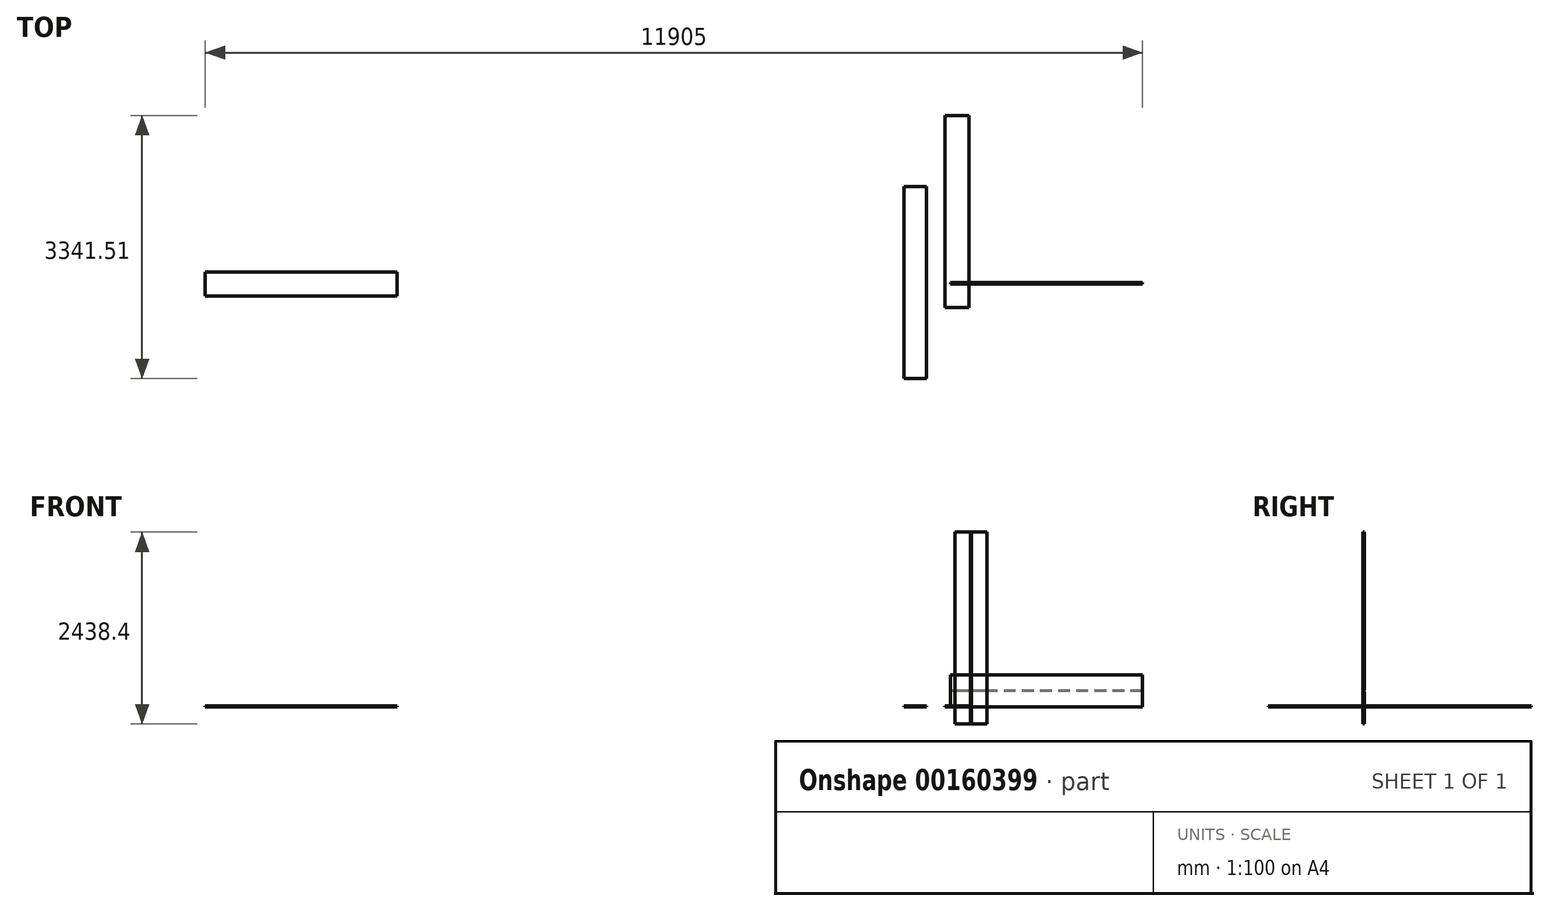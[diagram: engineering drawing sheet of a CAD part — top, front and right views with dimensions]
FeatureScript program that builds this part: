
annotation { "Feature Type Name" : "Feature", "Feature Type Description" : "" }
export const myFeature = defineFeature(function(context is Context, id is Id, definition is map)
    precondition{}
    {
        {
            var Q0;
            Q0=qCreatedBy(makeId("Top.planeOp"),FACE);
            var sketch = newSketch(context, id + "F0", { "sketchPlane" : qUnion([Q0])});
            skLineSegment(sketch, "E0.bottom", {"start": v(-311.98, 2122.24) * mm, "end": v(-7.18, 2122.24) * mm});
            skLineSegment(sketch, "E0.top", {"start": v(-311.98, -316.16) * mm, "end": v(-7.18, -316.16) * mm});
            skLineSegment(sketch, "E0.left", {"start": v(-311.98, 2122.24) * mm, "end": v(-311.98, -316.16) * mm});
            skLineSegment(sketch, "E0.right", {"start": v(-7.18, 2122.24) * mm, "end": v(-7.18, -316.16) * mm});
            skSolve(sketch);
        }
        {
            var Q0;
            Q0=makeQuery(id+"F0.imprint","IMPRINT",FACE,{"disambiguationData":[TD([[makeQuery(id+"F0.imprint","IMPRINT",EDGE,{"derivedFrom":sQuery(id+"F0.wireOp",EDGE,"E0.bottom")}),-1.0]])]});
            extrude(context, id + "F1", {"entities" : qUnion([Q0]), "depth" : 12.7 * mm});
        }
        {
            var Q0;
            Q0=qCreatedBy(makeId("Top.planeOp"),FACE);
            var sketch = newSketch(context, id + "F2", { "sketchPlane" : qUnion([Q0])});
            skLineSegment(sketch, "E1.bottom", {"start": v(-9710.38, -172.02) * mm, "end": v(-7271.98, -172.02) * mm});
            skLineSegment(sketch, "E1.top", {"start": v(-9710.38, 132.78) * mm, "end": v(-7271.98, 132.78) * mm});
            skLineSegment(sketch, "E1.left", {"start": v(-9710.38, -172.02) * mm, "end": v(-9710.38, 132.78) * mm});
            skLineSegment(sketch, "E1.right", {"start": v(-7271.98, -172.02) * mm, "end": v(-7271.98, 132.78) * mm});
            skSolve(sketch);
        }
        {
            var Q0;
            Q0 = qSketchRegion(id + "F2", true);
            extrude(context, id + "F3", {"entities" : qUnion([Q0]), "depth" : 12.7 * mm});
        }
        {
            var Q0;
            Q0=qCreatedBy(makeId("Front.planeOp"),FACE);
            var sketch = newSketch(context, id + "F4", { "sketchPlane" : qUnion([Q0])});
            skLineSegment(sketch, "E2.bottom", {"start": v(221, 2220.65) * mm, "end": v(-185.4, 2220.65) * mm});
            skLineSegment(sketch, "E2.top", {"start": v(221, -217.75) * mm, "end": v(-185.4, -217.75) * mm});
            skLineSegment(sketch, "E2.left", {"start": v(221, 2220.65) * mm, "end": v(221, -217.75) * mm});
            skLineSegment(sketch, "E2.right", {"start": v(-185.4, 2220.65) * mm, "end": v(-185.4, -217.75) * mm});
            skSolve(sketch);
        }
        {
            var Q0;
            Q0 = qSketchRegion(id + "F4", true);
            extrude(context, id + "F5", {"entities" : qUnion([Q0]), "depth" : 19.05 * mm});
        }
        {
            var Q0;
            Q0=makeQuery(id+"F5.opExtrude","CAP_FACE",FACE,{"disambiguationData":[OSD([sQuery(id+"F4.wireOp",EDGE,"E2.bottom"),sQuery(id+"F4.wireOp",EDGE,"E2.top"),sQuery(id+"F4.wireOp",EDGE,"E2.left"),sQuery(id+"F4.wireOp",EDGE,"E2.right")])],"isStart":false});
            var sketch = newSketch(context, id + "F6", { "sketchPlane" : qUnion([Q0])});
            skLineSegment(sketch, "E3.0", {"start": v(24.14, 2220.65) * mm, "end": v(24.14, -217.75) * mm});
            skLineSegment(sketch, "E4.0", {"start": v(11.44, 2220.65) * mm, "end": v(11.44, -217.75) * mm});
            skLineSegment(sketch, "E5", {"start": v(24.14, 2220.65) * mm, "end": v(11.44, 2220.65) * mm});
            skLineSegment(sketch, "E6", {"start": v(24.14, -217.75) * mm, "end": v(11.44, -217.75) * mm});
            skSolve(sketch);
        }
        {
            var Q0;
            Q0 = qSketchRegion(id + "F6", true);
            extrude(context, id + "F7", {"entities" : qUnion([Q0]), "operationType" : NewBodyOperationType.REMOVE, "oppositeDirection" : true, "depth" : 9.52 * mm});
        }
        {
            var Q0;
            Q0=qCreatedBy(makeId("Front.planeOp"),FACE);
            var sketch = newSketch(context, id + "F8", { "sketchPlane" : qUnion([Q0])});
            skLineSegment(sketch, "E7.bottom", {"start": v(2194.6, 406.4) * mm, "end": v(-243.8, 406.4) * mm});
            skLineSegment(sketch, "E7.top", {"start": v(2194.6, 0) * mm, "end": v(-243.8, 0) * mm});
            skLineSegment(sketch, "E7.left", {"start": v(2194.6, 406.4) * mm, "end": v(2194.6, 0) * mm});
            skLineSegment(sketch, "E7.right", {"start": v(-243.8, 406.4) * mm, "end": v(-243.8, 0) * mm});
            skLineSegment(sketch, "E8.0", {"start": v(2194.6, 209.55) * mm, "end": v(-243.8, 209.55) * mm});
            skLineSegment(sketch, "E9.0", {"start": v(2194.6, 196.85) * mm, "end": v(-243.8, 196.85) * mm});
            skLineSegment(sketch, "E10", {"start": v(2194.6, 209.55) * mm, "end": v(2194.6, 196.85) * mm});
            skLineSegment(sketch, "E11", {"start": v(-243.8, 209.55) * mm, "end": v(-243.8, 196.85) * mm});
            skSolve(sketch);
        }
        {
            var Q0;
            Q0 = qSketchRegion(id + "F8", true);
            extrude(context, id + "F9", {"entities" : qUnion([Q0]), "depth" : 19.05 * mm});
        }
        {
            var Q0;
            Q0=makeQuery(id+"F8.imprint","IMPRINT",FACE,{"disambiguationData":[TD([[makeQuery(id+"F8.imprint","IMPRINT",EDGE,{"derivedFrom":sQuery(id+"F8.wireOp",EDGE,"E8.0")}),1.0]])]});
            extrude(context, id + "F10", {"entities" : qUnion([Q0]), "operationType" : NewBodyOperationType.REMOVE, "depth" : 9.52 * mm});
        }
        {
            var Q0;
            Q0=qCreatedBy(makeId("Top.planeOp"),FACE);
            var sketch = newSketch(context, id + "F11", { "sketchPlane" : qUnion([Q0])});
            skLineSegment(sketch, "E12.bottom", {"start": v(-836.67, -1219.27) * mm, "end": v(-550.92, -1219.27) * mm});
            skLineSegment(sketch, "E12.top", {"start": v(-836.67, 1219.13) * mm, "end": v(-550.92, 1219.13) * mm});
            skLineSegment(sketch, "E12.left", {"start": v(-836.67, -1219.27) * mm, "end": v(-836.67, 1219.13) * mm});
            skLineSegment(sketch, "E12.right", {"start": v(-550.92, -1219.27) * mm, "end": v(-550.92, 1219.13) * mm});
            skSolve(sketch);
        }
        {
            var Q0;
            Q0 = qSketchRegion(id + "F11", true);
            extrude(context, id + "F12", {"entities" : qUnion([Q0]), "depth" : 12.7 * mm});
        }
    });
